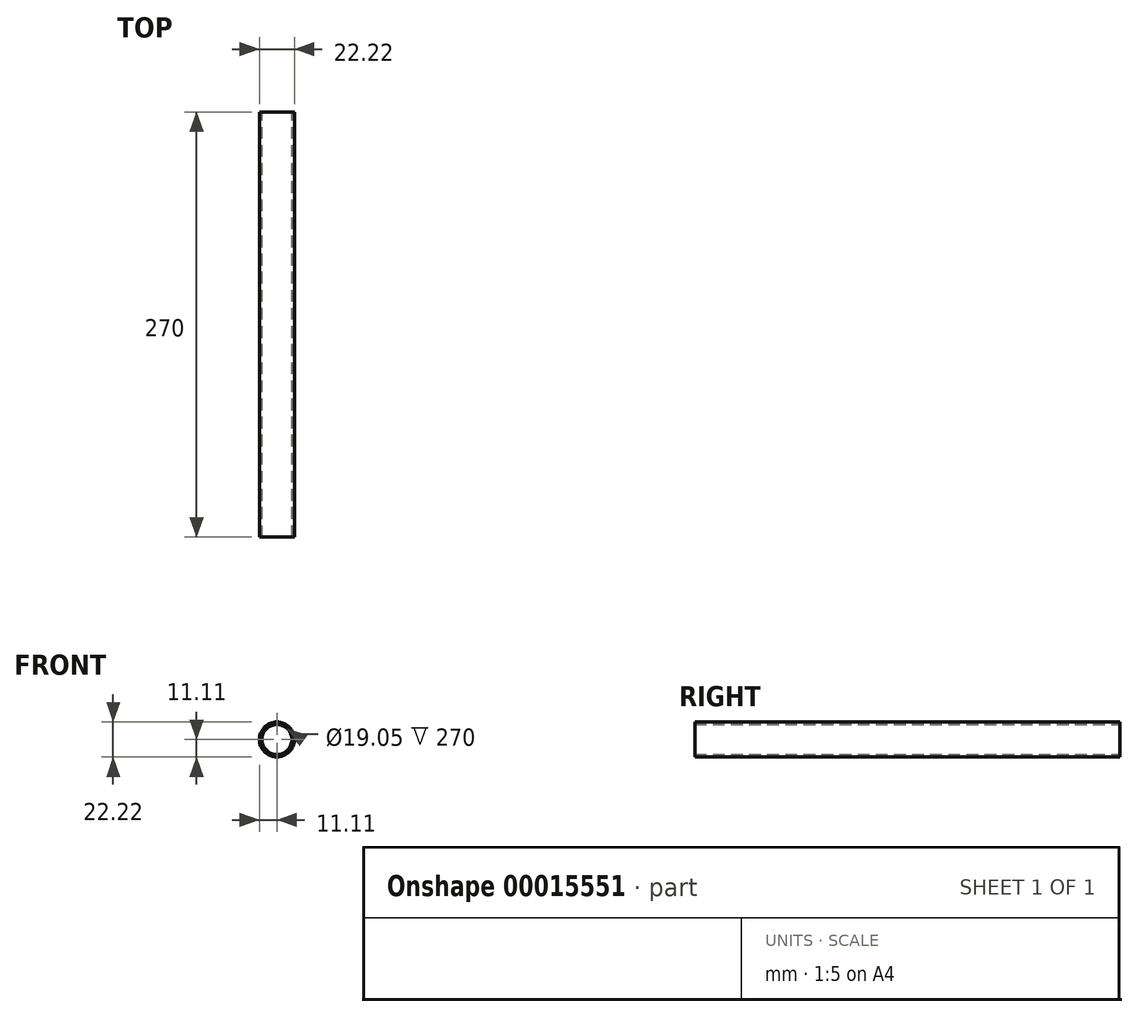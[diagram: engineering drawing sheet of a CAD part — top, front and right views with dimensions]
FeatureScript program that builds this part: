
annotation { "Feature Type Name" : "Feature", "Feature Type Description" : "" }
export const myFeature = defineFeature(function(context is Context, id is Id, definition is map)
    precondition{}
    {
        {
            var Q0;
            Q0=qCreatedBy(makeId("Front.planeOp"),FACE);
            var sketch = newSketch(context, id + "F0", { "sketchPlane" : qUnion([Q0])});
            skCircle(sketch, "E0", {"center": v(0, 0) * mm, "radius": 9.53 * mm});
            skCircle(sketch, "E1", {"center": v(0, 0) * mm, "radius": 11.11 * mm});
            skSolve(sketch);
        }
        {
            var Q0;
            Q0=makeQuery(id+"F0.imprint","IMPRINT",FACE,{"disambiguationData":[TD([[makeQuery(id+"F0.imprint","IMPRINT",EDGE,{"derivedFrom":sQuery(id+"F0.wireOp",EDGE,"E0")}),-1.0]])]});
            extrude(context, id + "F1", {"entities" : qUnion([Q0]), "depth" : 270 * mm});
        }
    });
